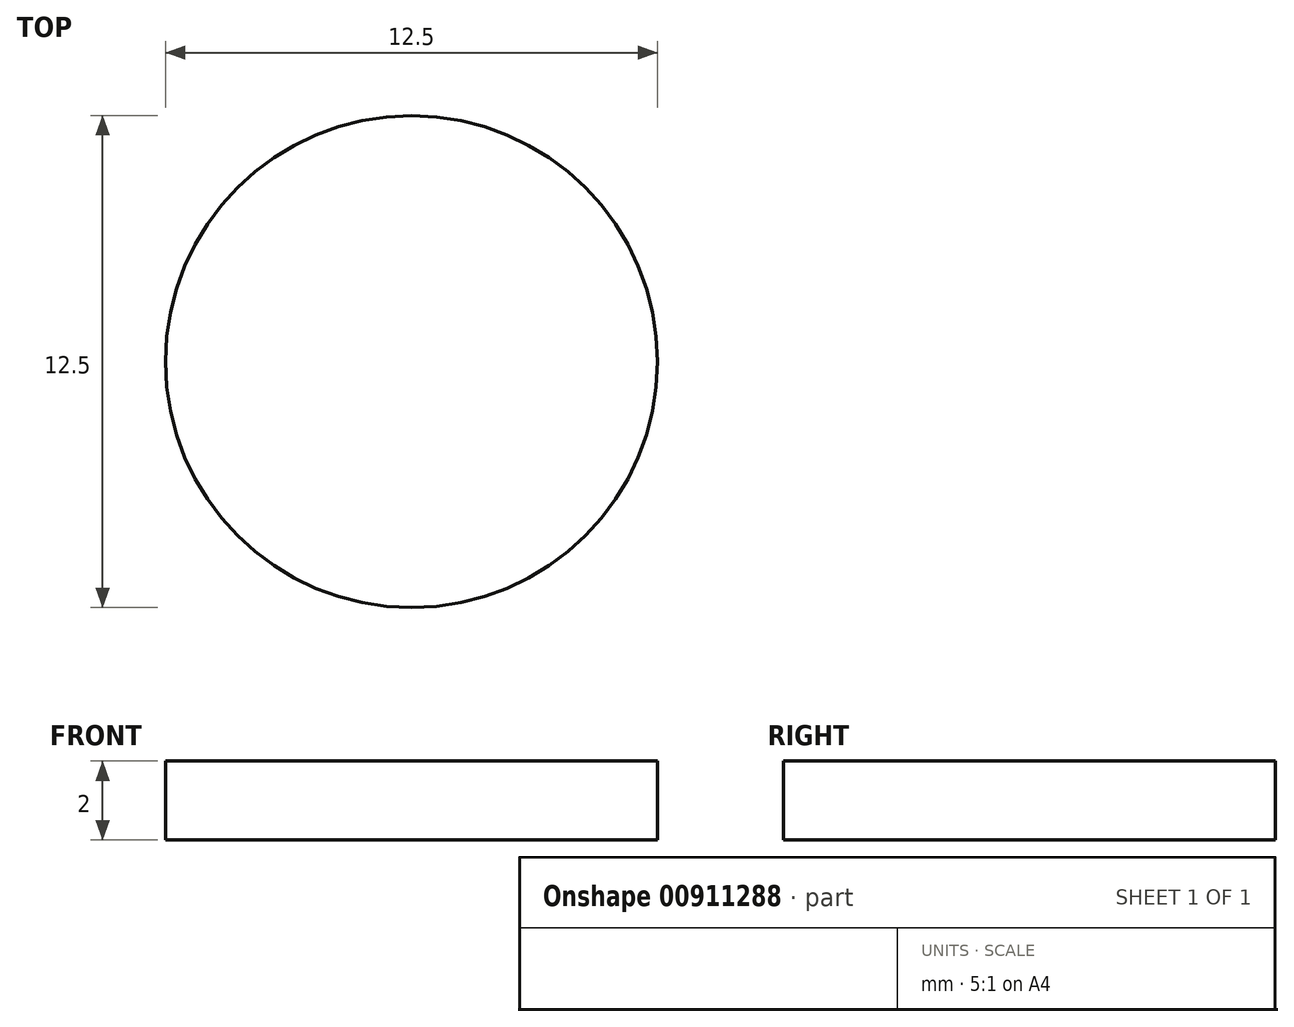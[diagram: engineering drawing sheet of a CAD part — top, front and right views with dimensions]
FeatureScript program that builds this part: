
annotation { "Feature Type Name" : "Feature", "Feature Type Description" : "" }
export const myFeature = defineFeature(function(context is Context, id is Id, definition is map)
    precondition{}
    {
        {
            var Q0;
            Q0=qCreatedBy(makeId("Top.planeOp"),FACE);
            var sketch = newSketch(context, id + "F0", { "sketchPlane" : qUnion([Q0])});
            skCircle(sketch, "E0", {"center": v(0, 0) * mm, "radius": 6.25 * mm});
            skSolve(sketch);
        }
        {
            var Q0;
            Q0=makeQuery(id+"F0.imprint","IMPRINT",FACE,{"disambiguationData":[TD([[makeQuery(id+"F0.imprint","IMPRINT",EDGE,{"derivedFrom":sQuery(id+"F0.wireOp",EDGE,"E0")}),1.0]])]});
            extrude(context, id + "F1", {"entities" : qUnion([Q0]), "depth" : 2 * mm, "offsetDistance" : 25 * mm});
        }
    });
